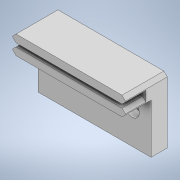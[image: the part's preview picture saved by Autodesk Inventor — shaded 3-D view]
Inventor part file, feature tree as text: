
AUTODESK INVENTOR PART (.ipt)
format: ipt  version: 2020.4 (Build 244396010, 396A)  size: 165,888 bytes
history: native  units: mm
features: sketch x5, extrude x4, chamfer x1, hole x1
ambient origin geometry x8: Origin, YZ Plane, XZ Plane, XY Plane, X Axis, Y Axis, Z Axis, Center Point
bodies: Solid1 (feature_tree)
feature tree (11):
  extrude  "Extrusion1"  Depth=38.0mm
  extrude  "Extrusion2"  Depth=2.0mm
  extrude  "Extrusion3"  Depth=12.0mm
  extrude  "Extrusion4"  Depth=27.0mm
  chamfer  "Chamfer1"  Distance=4.5mm
  hole  "Hole1"  [1 undecoded]
  sketch  "Sketch1"  dims[d0=66.0mm d1=38.0mm]
  sketch  "Sketch2"  dims[d2=9.5mm d3=0.0mm d4=2.0mm]
  sketch  "Sketch3"  dims[d5=2.0mm d6=12.0mm]
  sketch  "Sketch4"  dims[d7=7.0mm d8=0.0mm d9=27.0mm]
  sketch  "Sketch5"  dims[d10=2.0mm d11=4.5mm d12=15.0mm d13=0.0mm d14=3.0mm d15=0.0mm d16=2.0mm d17=2.0mm d18=45.0deg d19=11.0mm d20=11.0mm d21=44.0mm d22=11.1mm d23=19.05mm d24=5.5mm d25=6.0mm d26=8.5mm d27=5.0mm d28=90.0deg d29=8.0mm d30=20.594885mm]
note: 1 required parameter value undecoded (feature->parameter linkage not recoverable at this tier; creation-order binding heuristic only, values carry confidence <= 0.55)
